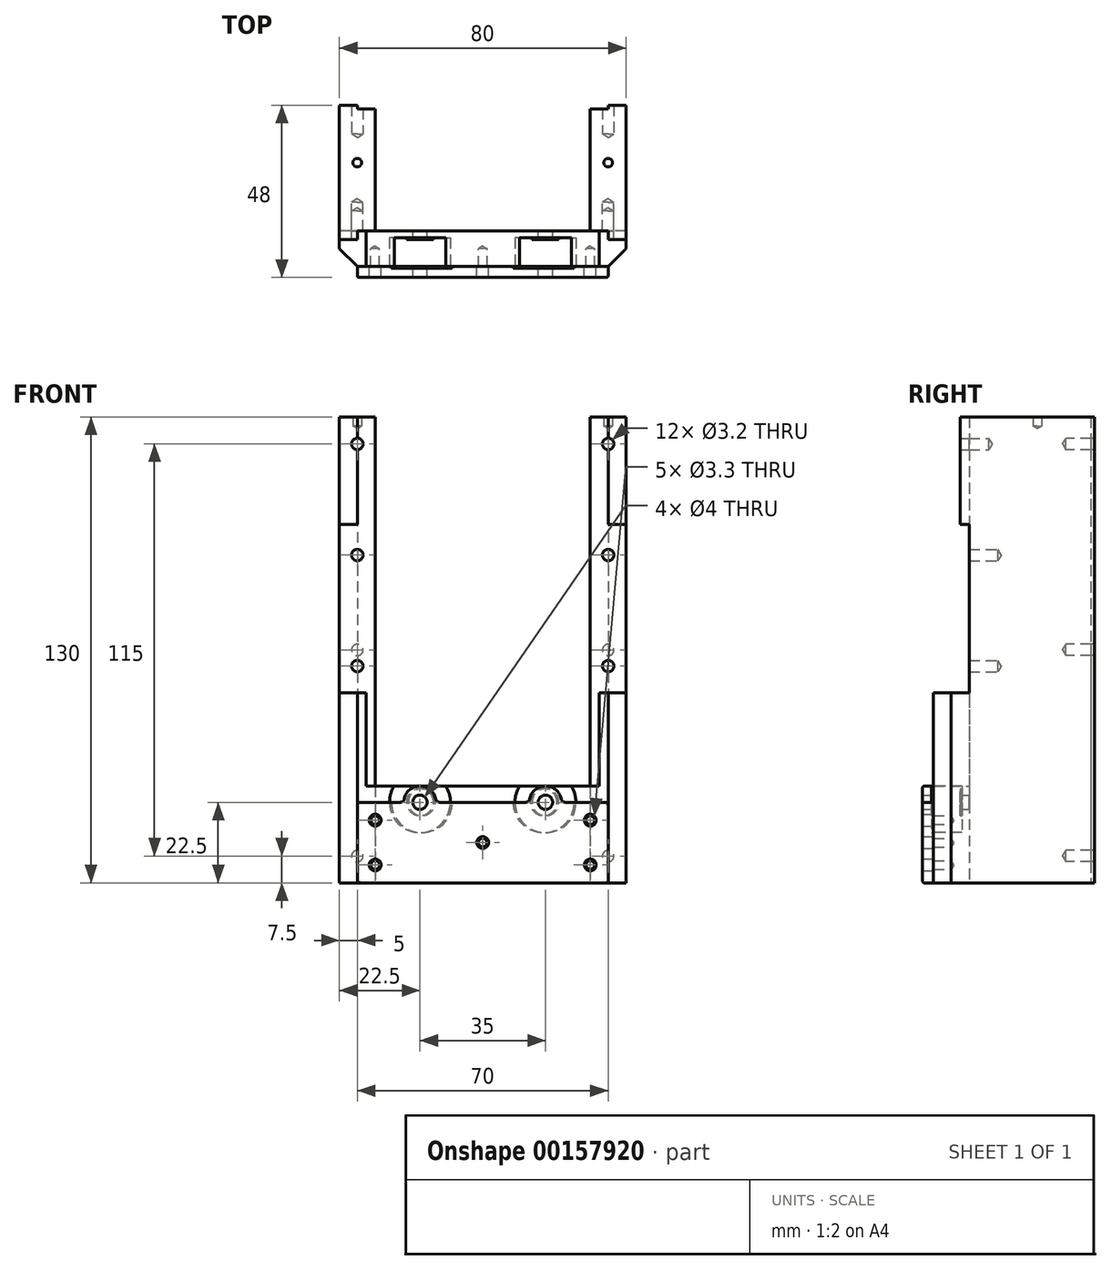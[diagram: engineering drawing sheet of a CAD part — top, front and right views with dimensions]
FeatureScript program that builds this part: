
annotation { "Feature Type Name" : "Feature", "Feature Type Description" : "" }
export const myFeature = defineFeature(function(context is Context, id is Id, definition is map)
    precondition{}
    {
        {
            var Q0;
            Q0=qCreatedBy(makeId("Top.planeOp"),FACE);
            cPlane(context, id + "F0", {"entities" : qUnion([Q0]), "cplaneType" : CPlaneType.OFFSET, "offset" : 90 * mm, "oppositeDirection" : true, "width" : 150 * mm, "height" : 150 * mm});
        }
        {
            var Q0;
            Q0=qCreatedBy(id+"F0.planeOp",FACE);
            var sketch = newSketch(context, id + "F1", { "sketchPlane" : qUnion([Q0])});
            skLineSegment(sketch, "E0", {"start": v(-30, -14.78) * mm, "end": v(30, -14.78) * mm});
            skLineSegment(sketch, "E1", {"start": v(40, -24.78) * mm, "end": v(-40, -24.78) * mm});
            skLineSegment(sketch, "E2.0", {"start": v(40, 20.22) * mm, "end": v(35, 20.22) * mm});
            skLineSegment(sketch, "E3", {"start": v(35, 20.22) * mm, "end": v(35, 19.22) * mm});
            skLineSegment(sketch, "E4", {"start": v(35, 19.22) * mm, "end": v(30, 19.22) * mm});
            skLineSegment(sketch, "E5", {"start": v(30, -14.78) * mm, "end": v(30, 19.22) * mm});
            skLineSegment(sketch, "E6.MirrorCS", {"start": v(-30, -14.78) * mm, "end": v(-30, 19.22) * mm});
            skLineSegment(sketch, "E7.MirrorCS", {"start": v(-40, 20.22) * mm, "end": v(-35, 20.22) * mm});
            skLineSegment(sketch, "E8", {"start": v(40, 20.22) * mm, "end": v(40, -24.78) * mm});
            skLineSegment(sketch, "E9", {"start": v(-30, 19.22) * mm, "end": v(-35, 19.22) * mm});
            skLineSegment(sketch, "E10", {"start": v(-35, 19.22) * mm, "end": v(-35, 20.22) * mm});
            skLineSegment(sketch, "E11", {"start": v(-40, 20.22) * mm, "end": v(-40, -24.78) * mm});
            skSolve(sketch);
        }
        {
            var Q0;
            Q0 = qSketchRegion(id + "F1", true);
            extrude(context, id + "F2", {"entities" : qUnion([Q0]), "depth" : 27 * mm});
        }
        {
            var Q0;
            Q0=makeQuery(id+"F2.opExtrude","CAP_FACE",FACE,{"disambiguationData":[OSD([sQuery(id+"F1.wireOp",EDGE,"E0"),sQuery(id+"F1.wireOp",EDGE,"E1"),sQuery(id+"F1.wireOp",EDGE,"E2.0"),sQuery(id+"F1.wireOp",EDGE,"E3"),sQuery(id+"F1.wireOp",EDGE,"E4"),sQuery(id+"F1.wireOp",EDGE,"E5"),sQuery(id+"F1.wireOp",EDGE,"E6.MirrorCS"),sQuery(id+"F1.wireOp",EDGE,"E7.MirrorCS"),sQuery(id+"F1.wireOp",EDGE,"E8"),sQuery(id+"F1.wireOp",EDGE,"E9"),sQuery(id+"F1.wireOp",EDGE,"E10"),sQuery(id+"F1.wireOp",EDGE,"E11")])],"isStart":false});
            var sketch = newSketch(context, id + "F3", { "sketchPlane" : qUnion([Q0])});
            skLineSegment(sketch, "E12.0", {"start": v(40, 20.22) * mm, "end": v(40, -24.78) * mm});
            skLineSegment(sketch, "E13.0", {"start": v(40, 20.22) * mm, "end": v(35, 20.22) * mm});
            skLineSegment(sketch, "E14.0", {"start": v(35, 19.22) * mm, "end": v(30, 19.22) * mm});
            skLineSegment(sketch, "E15", {"start": v(35, 20.22) * mm, "end": v(35, 19.22) * mm});
            skLineSegment(sketch, "E16.0", {"start": v(30, -14.78) * mm, "end": v(30, 19.22) * mm});
            skLineSegment(sketch, "E17", {"start": v(40, -24.78) * mm, "end": v(32.5, -24.78) * mm});
            skLineSegment(sketch, "E18", {"start": v(32.5, -24.78) * mm, "end": v(32.5, -14.78) * mm});
            skLineSegment(sketch, "E19.MirrorCS", {"start": v(-30, -14.78) * mm, "end": v(-30, 19.22) * mm});
            skLineSegment(sketch, "E20.MirrorCS", {"start": v(-35, 19.22) * mm, "end": v(-30, 19.22) * mm});
            skLineSegment(sketch, "E21.MirrorCS", {"start": v(-40, 20.22) * mm, "end": v(-35, 20.22) * mm});
            skLineSegment(sketch, "E22.MirrorCS", {"start": v(-40, 20.22) * mm, "end": v(-40, -24.78) * mm});
            skLineSegment(sketch, "E23.MirrorCS", {"start": v(-40, -24.78) * mm, "end": v(-32.5, -24.78) * mm});
            skLineSegment(sketch, "E24.MirrorCS", {"start": v(-32.5, -24.78) * mm, "end": v(-32.5, -14.78) * mm});
            skLineSegment(sketch, "E25", {"start": v(-35, 20.22) * mm, "end": v(-35, 19.22) * mm});
            skLineSegment(sketch, "E26", {"start": v(-32.5, -14.78) * mm, "end": v(32.5, -14.78) * mm});
            skSolve(sketch);
        }
        {
            var Q0;
            Q0 = qSketchRegion(id + "F3", true);
            extrude(context, id + "F4", {"entities" : qUnion([Q0]), "operationType" : NewBodyOperationType.ADD, "depth" : 26 * mm});
        }
        {
            var Q0;
            Q0=makeQuery(id+"F4.opExtrude","CAP_FACE",FACE,{"disambiguationData":[OSD([sQuery(id+"F3.wireOp",EDGE,"E19.MirrorCS"),sQuery(id+"F3.wireOp",EDGE,"E20.MirrorCS"),sQuery(id+"F3.wireOp",EDGE,"E21.MirrorCS"),sQuery(id+"F3.wireOp",EDGE,"E22.MirrorCS"),sQuery(id+"F3.wireOp",EDGE,"E23.MirrorCS"),sQuery(id+"F3.wireOp",EDGE,"E24.MirrorCS"),sQuery(id+"F3.wireOp",EDGE,"E25"),sQuery(id+"F3.wireOp",EDGE,"E26")])],"isStart":false});
            var sketch = newSketch(context, id + "F5", { "sketchPlane" : qUnion([Q0])});
            skLineSegment(sketch, "E27.0", {"start": v(40, 20.22) * mm, "end": v(40, -14.78) * mm});
            skLineSegment(sketch, "E28.0", {"start": v(40, 20.22) * mm, "end": v(35, 20.22) * mm});
            skLineSegment(sketch, "E29.0", {"start": v(35, 19.22) * mm, "end": v(30, 19.22) * mm});
            skLineSegment(sketch, "E30.0", {"start": v(30, -14.78) * mm, "end": v(30, 19.22) * mm});
            skLineSegment(sketch, "E31", {"start": v(35, 20.22) * mm, "end": v(35, 19.22) * mm});
            skLineSegment(sketch, "E32.MirrorCS", {"start": v(-40, 20.22) * mm, "end": v(-40, -14.78) * mm});
            skLineSegment(sketch, "E33.MirrorCS", {"start": v(-40, 20.22) * mm, "end": v(-35, 20.22) * mm});
            skLineSegment(sketch, "E34.MirrorCS", {"start": v(-35, 19.22) * mm, "end": v(-30, 19.22) * mm});
            skLineSegment(sketch, "E35.MirrorCS", {"start": v(-30, -14.78) * mm, "end": v(-30, 19.22) * mm});
            skLineSegment(sketch, "E36.MirrorCS", {"start": v(-35, 20.22) * mm, "end": v(-35, 19.22) * mm});
            skLineSegment(sketch, "E37", {"start": v(40, -14.78) * mm, "end": v(30, -14.78) * mm});
            skPoint(sketch, "E38.orphan", {"position": v(40, -24.78) * mm});
            skPoint(sketch, "E39.orphan", {"position": v(-40, -24.78) * mm});
            skLineSegment(sketch, "E40.trimOffspring", {"start": v(-30, -14.78) * mm, "end": v(-40, -14.78) * mm});
            skSolve(sketch);
        }
        {
            var Q0;
            Q0 = qSketchRegion(id + "F5", true);
            extrude(context, id + "F6", {"entities" : qUnion([Q0]), "operationType" : NewBodyOperationType.ADD, "depth" : 47 * mm});
        }
        {
            var Q0;
            Q0=makeQuery(id+"F6.opExtrude","CAP_FACE",FACE,{"disambiguationData":[OSD([sQuery(id+"F5.wireOp",EDGE,"E27.0"),sQuery(id+"F5.wireOp",EDGE,"E28.0"),sQuery(id+"F5.wireOp",EDGE,"E29.0"),sQuery(id+"F5.wireOp",EDGE,"E30.0"),sQuery(id+"F5.wireOp",EDGE,"E31"),sQuery(id+"F5.wireOp",EDGE,"E37")])],"isStart":false});
            var sketch = newSketch(context, id + "F7", { "sketchPlane" : qUnion([Q0])});
            skLineSegment(sketch, "E41.0", {"start": v(40, 20.22) * mm, "end": v(35, 20.22) * mm});
            skLineSegment(sketch, "E42.0", {"start": v(35, 19.22) * mm, "end": v(30, 19.22) * mm});
            skLineSegment(sketch, "E43.0", {"start": v(30, -14.78) * mm, "end": v(30, 19.22) * mm});
            skLineSegment(sketch, "E44.0", {"start": v(35, -14.78) * mm, "end": v(30, -14.78) * mm});
            skLineSegment(sketch, "E45", {"start": v(35, 20.22) * mm, "end": v(35, 19.22) * mm});
            skLineSegment(sketch, "E46", {"start": v(35, -14.78) * mm, "end": v(35, -17.28) * mm});
            skLineSegment(sketch, "E47", {"start": v(35, -17.28) * mm, "end": v(40, -17.28) * mm});
            skPoint(sketch, "E48.orphan", {"position": v(40, -14.78) * mm});
            skLineSegment(sketch, "E49", {"start": v(40, 20.22) * mm, "end": v(40, -17.28) * mm});
            skLineSegment(sketch, "E50.MirrorCS", {"start": v(-35, 19.22) * mm, "end": v(-30, 19.22) * mm});
            skLineSegment(sketch, "E51.MirrorCS", {"start": v(-35, 20.22) * mm, "end": v(-35, 19.22) * mm});
            skLineSegment(sketch, "E52.MirrorCS", {"start": v(-40, 20.22) * mm, "end": v(-35, 20.22) * mm});
            skLineSegment(sketch, "E53.MirrorCS", {"start": v(-40, 20.22) * mm, "end": v(-40, -17.28) * mm});
            skLineSegment(sketch, "E54.MirrorCS", {"start": v(-35, -17.28) * mm, "end": v(-40, -17.28) * mm});
            skLineSegment(sketch, "E55.MirrorCS", {"start": v(-35, -14.78) * mm, "end": v(-35, -17.28) * mm});
            skLineSegment(sketch, "E56.MirrorCS", {"start": v(-35, -14.78) * mm, "end": v(-30, -14.78) * mm});
            skLineSegment(sketch, "E57.MirrorCS", {"start": v(-30, -14.78) * mm, "end": v(-30, 19.22) * mm});
            skSolve(sketch);
        }
        {
            var Q0;
            Q0 = qSketchRegion(id + "F7", true);
            extrude(context, id + "F8", {"entities" : qUnion([Q0]), "operationType" : NewBodyOperationType.ADD, "depth" : 30 * mm});
        }
        {
            var Q0;
            Q0=makeQuery(id+"F4.boolean.opBoolean","MERGE",FACE,{"derivedFrom":[makeQuery(id+"F2.opExtrude","SWEPT_FACE",FACE,{"disambiguationData":[OSD([sQuery(id+"F1.wireOp",EDGE,"E1")])]}),makeQuery(id+"F4.opExtrude","SWEPT_FACE",FACE,{"disambiguationData":[OSD([sQuery(id+"F3.wireOp",EDGE,"E17")])]}),makeQuery(id+"F4.opExtrude","SWEPT_FACE",FACE,{"disambiguationData":[OSD([sQuery(id+"F3.wireOp",EDGE,"E23.MirrorCS")])]})]});
            var sketch = newSketch(context, id + "F9", { "sketchPlane" : qUnion([Q0])});
            skCircle(sketch, "E58", {"center": v(17.5, -67.5) * mm, "radius": 8.5 * mm});
            skCircle(sketch, "E59.MirrorC", {"center": v(-17.5, -67.5) * mm, "radius": 8.5 * mm});
            skSolve(sketch);
        }
        {
            var Q0;
            Q0 = qSketchRegion(id + "F9", true);
            extrude(context, id + "F10", {"entities" : qUnion([Q0]), "operationType" : NewBodyOperationType.REMOVE, "oppositeDirection" : true, "depth" : 8 * mm});
        }
        {
            var Q0;
            Q0=makeQuery(id+"F10.boolean.opBoolean","COPY",FACE,{"derivedFrom":makeQuery(id+"F10.opExtrude","CAP_FACE",FACE,{"disambiguationData":[OSD([sQuery(id+"F9.wireOp",EDGE,"E58")])],"isStart":false})});
            var sketch = newSketch(context, id + "F11", { "sketchPlane" : qUnion([Q0])});
            skCircle(sketch, "E60", {"center": v(17.5, -67.5) * mm, "radius": 2 * mm});
            skCircle(sketch, "E61", {"center": v(17.5, -67.5) * mm, "radius": 3.75 * mm});
            skCircle(sketch, "E62.MirrorC", {"center": v(-17.5, -67.5) * mm, "radius": 3.75 * mm});
            skCircle(sketch, "E63.MirrorC", {"center": v(-17.5, -67.5) * mm, "radius": 2 * mm});
            skSolve(sketch);
        }
        {
            var Q0;
            Q0 = qSketchRegion(id + "F11", true);
            extrude(context, id + "F12", {"entities" : qUnion([Q0]), "operationType" : NewBodyOperationType.ADD, "depth" : 0.5 * mm});
        }
        {
            var Q0;
            Q0=makeQuery(id+"F12.boolean.opBoolean","SPLIT",FACE,{"disambiguationData":[TD([makeQuery(id+"F12.opExtrude","SWEPT_FACE",FACE,{"disambiguationData":[OSD([sQuery(id+"F11.wireOp",EDGE,"E60")])]})])],"derivedFrom":makeQuery(id+"F10.boolean.opBoolean","COPY",FACE,{"derivedFrom":makeQuery(id+"F10.opExtrude","CAP_FACE",FACE,{"disambiguationData":[OSD([sQuery(id+"F9.wireOp",EDGE,"E58")])],"isStart":false})})});
            var Q1;
            Q1=makeQuery(id+"F12.boolean.opBoolean","SPLIT",FACE,{"disambiguationData":[TD([makeQuery(id+"F12.opExtrude","SWEPT_FACE",FACE,{"disambiguationData":[OSD([sQuery(id+"F11.wireOp",EDGE,"E63.MirrorC")])]})])],"derivedFrom":makeQuery(id+"F10.boolean.opBoolean","COPY",FACE,{"derivedFrom":makeQuery(id+"F10.opExtrude","CAP_FACE",FACE,{"disambiguationData":[OSD([sQuery(id+"F9.wireOp",EDGE,"E59.MirrorC")])],"isStart":false})})});
            extrude(context, id + "F13", {"entities" : qUnion([Q0, Q1]), "operationType" : NewBodyOperationType.REMOVE, "oppositeDirection" : true, "depth" : 25 * mm});
        }
        {
            var Q0;
            Q0=makeQuery(id+"F4.boolean.opBoolean","MERGE",EDGE,{"derivedFrom":[makeQuery(id+"F2.opExtrude","SWEPT_EDGE",EDGE,{"disambiguationData":[OSD([sQuery(id+"F1.wireOp",EDGE,"E1"),sQuery(id+"F1.wireOp",EDGE,"E8")])]}),makeQuery(id+"F4.opExtrude","SWEPT_EDGE",EDGE,{"disambiguationData":[OSD([sQuery(id+"F3.wireOp",EDGE,"E12.0"),sQuery(id+"F3.wireOp",EDGE,"E17")])]})]});
            var Q1;
            Q1=makeQuery(id+"F4.boolean.opBoolean","MERGE",EDGE,{"derivedFrom":[makeQuery(id+"F2.opExtrude","SWEPT_EDGE",EDGE,{"disambiguationData":[OSD([sQuery(id+"F1.wireOp",EDGE,"E1"),sQuery(id+"F1.wireOp",EDGE,"E11")])]}),makeQuery(id+"F4.opExtrude","SWEPT_EDGE",EDGE,{"disambiguationData":[OSD([sQuery(id+"F3.wireOp",EDGE,"E22.MirrorCS"),sQuery(id+"F3.wireOp",EDGE,"E23.MirrorCS")])]})]});
            chamfer(context, id + "F14", {"entities" : qUnion([Q0, Q1]), "width" : 5 * mm, "tangentPropagation" : true});
        }
        {
            var Q0;
            Q0=makeQuery(id+"F14.opChamfer","SPLIT",FACE,{"disambiguationData":[OD(2.0)],"derivedFrom":makeQuery(id+"F4.boolean.opBoolean","MERGE",FACE,{"derivedFrom":[makeQuery(id+"F2.opExtrude","SWEPT_FACE",FACE,{"disambiguationData":[OSD([sQuery(id+"F1.wireOp",EDGE,"E1")])]}),makeQuery(id+"F4.opExtrude","SWEPT_FACE",FACE,{"disambiguationData":[OSD([sQuery(id+"F3.wireOp",EDGE,"E17")])]}),makeQuery(id+"F4.opExtrude","SWEPT_FACE",FACE,{"disambiguationData":[OSD([sQuery(id+"F3.wireOp",EDGE,"E23.MirrorCS")])]})]})});
            var sketch = newSketch(context, id + "F15", { "sketchPlane" : qUnion([Q0])});
            skCircle(sketch, "E64.0", {"center": v(-17.5, -67.5) * mm, "radius": 2 * mm});
            skCircle(sketch, "E65.0", {"center": v(17.5, -67.5) * mm, "radius": 2 * mm});
            skLineSegment(sketch, "E66", {"start": v(-35, -90) * mm, "end": v(35, -90) * mm});
            skLineSegment(sketch, "E67", {"start": v(35, -90) * mm, "end": v(35, -67.5) * mm});
            skPoint(sketch, "E68.orphan", {"position": v(-35, -70.15) * mm});
            skPoint(sketch, "E69.orphan", {"position": v(35, -70.15) * mm});
            skLineSegment(sketch, "E70.MirrorCS", {"start": v(-35, -90) * mm, "end": v(-35, -67.5) * mm});
            skLineSegment(sketch, "E71", {"start": v(-35, -67.5) * mm, "end": v(-22, -67.5) * mm});
            skArc(sketch, "E72", {"start": v(22, -67.5) * mm, "mid": v(17.5, -63) * mm, "end": v(13, -67.5) * mm});
            skArc(sketch, "E73.MirrorC", {"start": v(-22, -67.5) * mm, "mid": v(-17.5, -63) * mm, "end": v(-13, -67.5) * mm});
            skLineSegment(sketch, "E74.trimOffspring", {"start": v(-13, -67.5) * mm, "end": v(13, -67.5) * mm});
            skLineSegment(sketch, "E75.trimOffspring", {"start": v(19.5, -67.5) * mm, "end": v(35, -67.5) * mm});
            skSolve(sketch);
        }
        {
            var Q0;
            Q0 = qSketchRegion(id + "F15", true);
            extrude(context, id + "F16", {"entities" : qUnion([Q0]), "depth" : 3 * mm});
        }
        {
            var Q0;
            Q0=makeQuery(id+"F16.opExtrude","CAP_FACE",FACE,{"disambiguationData":[OSD([sQuery(id+"F15.wireOp",EDGE,"E64.0"),sQuery(id+"F15.wireOp",EDGE,"E65.0"),sQuery(id+"F15.wireOp",EDGE,"2QbMT2nW-IAl8-gtQJ-p2Iz-kW7memZSLAfn"),sQuery(id+"F15.wireOp",EDGE,"XE8XkPs4-BKOY-PGEx-oHFn-p07Z73GzMPRD"),sQuery(id+"F15.wireOp",EDGE,"nKjhpJZj-CjEx-POrg-9XYW-dTicIIr4c24b"),sQuery(id+"F15.wireOp",EDGE,"gEchJP0V-37SP-750J-l0El-UBUOQwK3IVrr"),sQuery(id+"F15.wireOp",EDGE,"E66"),sQuery(id+"F15.wireOp",EDGE,"h1sLuy6x-Yomr-532m-xEHi-TijXeizuQsZO"),sQuery(id+"F15.wireOp",EDGE,"mAC8uAtB-FTIW-m3pB-ZDK8-pyVDg6E0Xd48"),sQuery(id+"F15.wireOp",EDGE,"HEceFARl-BTcW-MZeQ-kquP-lKw35DMknYV2")])],"isStart":false});
            var sketch = newSketch(context, id + "F17", { "sketchPlane" : qUnion([Q0])});
            skCircle(sketch, "E76", {"center": v(0, -78.75) * mm, "radius": 2 * mm});
            skCircle(sketch, "E77", {"center": v(30, -85) * mm, "radius": 2 * mm});
            skCircle(sketch, "E78", {"center": v(30, -72.5) * mm, "radius": 2 * mm});
            skCircle(sketch, "E79.MirrorC", {"center": v(-30, -72.5) * mm, "radius": 2 * mm});
            skCircle(sketch, "E80.MirrorC", {"center": v(-30, -85) * mm, "radius": 2 * mm});
            skSolve(sketch);
        }
        {
            var Q0;
            Q0=makeQuery(id+"F4.boolean.opBoolean","MERGE",FACE,{"derivedFrom":[makeQuery(id+"F2.opExtrude","SWEPT_FACE",FACE,{"disambiguationData":[OSD([sQuery(id+"F1.wireOp",EDGE,"E1")])]}),makeQuery(id+"F4.opExtrude","SWEPT_FACE",FACE,{"disambiguationData":[OSD([sQuery(id+"F3.wireOp",EDGE,"E17")])]}),makeQuery(id+"F4.opExtrude","SWEPT_FACE",FACE,{"disambiguationData":[OSD([sQuery(id+"F3.wireOp",EDGE,"E23.MirrorCS")])]})]});
            var sketch = newSketch(context, id + "F18", { "sketchPlane" : qUnion([Q0])});
            skCircle(sketch, "E81", {"center": v(17, -67.5) * mm, "radius": 3.75 * mm});
            skCircle(sketch, "E82", {"center": v(17, -67.5) * mm, "radius": 8.5 * mm});
            skCircle(sketch, "E83.MirrorC", {"center": v(-17, -67.5) * mm, "radius": 8.5 * mm});
            skCircle(sketch, "E84.MirrorC", {"center": v(-17, -67.5) * mm, "radius": 3.75 * mm});
            skSolve(sketch);
        }
        {
            var Q0;
            Q0 = qSketchRegion(id + "F18", true);
            extrude(context, id + "F19", {"entities" : qUnion([Q0]), "operationType" : NewBodyOperationType.REMOVE, "depth" : 0.5 * mm});
        }
        {
            var Q0;
            Q0=makeQuery(id+"F8.boolean.opBoolean","MERGE",FACE,{"derivedFrom":[makeQuery(id+"F6.boolean.opBoolean","MERGE",FACE,{"derivedFrom":[makeQuery(id+"F4.boolean.opBoolean","MERGE",FACE,{"derivedFrom":[makeQuery(id+"F2.opExtrude","SWEPT_FACE",FACE,{"disambiguationData":[OSD([sQuery(id+"F1.wireOp",EDGE,"E7.MirrorCS")])]}),makeQuery(id+"F4.opExtrude","SWEPT_FACE",FACE,{"disambiguationData":[OSD([sQuery(id+"F3.wireOp",EDGE,"E21.MirrorCS")])]})]}),makeQuery(id+"F6.opExtrude","SWEPT_FACE",FACE,{"disambiguationData":[OSD([sQuery(id+"F5.wireOp",EDGE,"E33.MirrorCS")])]})]}),makeQuery(id+"F8.opExtrude","SWEPT_FACE",FACE,{"disambiguationData":[OSD([sQuery(id+"F7.wireOp",EDGE,"E52.MirrorCS")])]})]});
            var sketch = newSketch(context, id + "F20", { "sketchPlane" : qUnion([Q0])});
            skCircle(sketch, "E85", {"center": v(35, -25) * mm, "radius": 3.68 * mm});
            skCircle(sketch, "E86", {"center": v(35, 32.5) * mm, "radius": 3.47 * mm});
            skCircle(sketch, "E87.MirrorC", {"center": v(-35, 32.5) * mm, "radius": 3.47 * mm});
            skCircle(sketch, "E88.MirrorC", {"center": v(-35, -25) * mm, "radius": 3.68 * mm});
            skLineSegment(sketch, "E89", {"start": v(-35, -25) * mm, "end": v(35, -25) * mm});
            skCircle(sketch, "E90.MirrorC", {"center": v(-35, -82.5) * mm, "radius": 3.47 * mm});
            skCircle(sketch, "E91.MirrorC", {"center": v(35, -82.5) * mm, "radius": 3.47 * mm});
            skSolve(sketch);
        }
        {
            var Q0;
            Q0=sQuery(id+"F20.wireOp",VERTEX,"E86.center");
            var Q1;
            Q1=sQuery(id+"F20.wireOp",VERTEX,"E85.center");
            var Q2;
            Q2=sQuery(id+"F20.wireOp",VERTEX,"4epNUfqm-IPoI-M6fA-UF52-nUd3HmOOQX4Y.center");
            var Q3;
            Q3=sQuery(id+"F20.wireOp",VERTEX,"a63e8368-61fe-4b29-9349-38a90727234b0.MirrorC.center");
            var Q4;
            Q4=sQuery(id+"F20.wireOp",VERTEX,"E88.MirrorC.center");
            var Q5;
            Q5=sQuery(id+"F20.wireOp",VERTEX,"E87.MirrorC.center");
            var Q6;
            Q6=sQuery(id+"F20.wireOp",VERTEX,"E90.MirrorC.center");
            var Q7;
            Q7=sQuery(id+"F20.wireOp",VERTEX,"E91.MirrorC.center");
            var Q8;
            Q8=makeQuery(id+"F2.opExtrude","SWEPT_BODY",BODY,{"disambiguationData":[OSD([sQuery(id+"F1.wireOp",EDGE,"E0"),sQuery(id+"F1.wireOp",EDGE,"E1"),sQuery(id+"F1.wireOp",EDGE,"E2.0"),sQuery(id+"F1.wireOp",EDGE,"E3"),sQuery(id+"F1.wireOp",EDGE,"E4"),sQuery(id+"F1.wireOp",EDGE,"E5"),sQuery(id+"F1.wireOp",EDGE,"E6.MirrorCS"),sQuery(id+"F1.wireOp",EDGE,"E7.MirrorCS"),sQuery(id+"F1.wireOp",EDGE,"E8"),sQuery(id+"F1.wireOp",EDGE,"E9"),sQuery(id+"F1.wireOp",EDGE,"E10"),sQuery(id+"F1.wireOp",EDGE,"E11")])]});
            hole(context, id + "F21", {"style" : HoleStyle.SIMPLE, "endStyle" : HoleEndStyle.BLIND, "standardTappedOrClearance" : lookupTablePath({ "standard" : "ISO", "engagement" : "75%", "pitch" : "0.75 mm", "size" : "M4", "type" : "Tapped" }), "standardBlindInLast" : lookupTablePath({ "standard" : "ISO", "engagement" : "75%", "pitch" : "0.75 mm", "size" : "M4", "type" : "Tapped" }), "holeDiameter" : 3.2 * mm, "holeDepth" : 8 * mm, "locations" : qUnion([Q0, Q1, Q2, Q3, Q4, Q5, Q6, Q7]), "scope" : qUnion([Q8]), "startStyle" : HoleStartStyle.SKETCH});
        }
        {
            var Q0;
            {var subQ0=sQuery(id+"F3.wireOp",EDGE,"E26");Q0=makeQuery(id+"F8.boolean.opBoolean","MERGE",FACE,{"derivedFrom":[makeQuery(id+"F6.boolean.opBoolean","MERGE",FACE,{"derivedFrom":[makeQuery(id+"F4.opExtrude","SWEPT_FACE",FACE,{"disambiguationData":[OSD([subQ0]),TDD([makeQuery(id+"F3.imprint","IMPRINT",EDGE,{"disambiguationData":[TD([[makeQuery(id+"F3.imprint","INTERSECT",VERTEX,{"derivedFrom":[sQuery(id+"F3.wireOp",EDGE,"E19.MirrorCS"),subQ0]}),1.0]])],"derivedFrom":subQ0})])]}),makeQuery(id+"F6.opExtrude","SWEPT_FACE",FACE,{"disambiguationData":[OSD([sQuery(id+"F5.wireOp",EDGE,"E40.trimOffspring")])]})]}),makeQuery(id+"F8.opExtrude","SWEPT_FACE",FACE,{"disambiguationData":[OSD([sQuery(id+"F7.wireOp",EDGE,"E56.MirrorCS")])]})]});}
            var sketch = newSketch(context, id + "F22", { "sketchPlane" : qUnion([Q0])});
            skCircle(sketch, "E92", {"center": v(-35, 1.5) * mm, "radius": 1.13 * mm});
            skCircle(sketch, "E93.MirrorC", {"center": v(35, 1.5) * mm, "radius": 1.13 * mm});
            skCircle(sketch, "E94", {"center": v(-35, -29.5) * mm, "radius": 1.45 * mm});
            skCircle(sketch, "E95.MirrorC", {"center": v(35, -29.5) * mm, "radius": 1.45 * mm});
            skSolve(sketch);
        }
        {
            var Q0;
            Q0=makeQuery(id+"F8.opExtrude","SWEPT_FACE",FACE,{"disambiguationData":[OSD([sQuery(id+"F7.wireOp",EDGE,"E54.MirrorCS")])]});
            var sketch = newSketch(context, id + "F23", { "sketchPlane" : qUnion([Q0])});
            skCircle(sketch, "E96", {"center": v(-35, 32.5) * mm, "radius": 2.04 * mm});
            skCircle(sketch, "E97.MirrorC", {"center": v(35, 32.5) * mm, "radius": 2.04 * mm});
            skSolve(sketch);
        }
        {
            var Q0;
            Q0=sQuery(id+"F23.wireOp",VERTEX,"E96.center");
            var Q1;
            Q1=sQuery(id+"F23.wireOp",VERTEX,"E97.MirrorC.center");
            var Q2;
            Q2=sQuery(id+"F22.wireOp",VERTEX,"E92.center");
            var Q3;
            Q3=sQuery(id+"F22.wireOp",VERTEX,"E93.MirrorC.center");
            var Q4;
            Q4=sQuery(id+"F22.wireOp",VERTEX,"E94.center");
            var Q5;
            Q5=sQuery(id+"F22.wireOp",VERTEX,"E95.MirrorC.center");
            var Q6;
            Q6=makeQuery(id+"F2.opExtrude","SWEPT_BODY",BODY,{"disambiguationData":[OSD([sQuery(id+"F1.wireOp",EDGE,"E0"),sQuery(id+"F1.wireOp",EDGE,"E1"),sQuery(id+"F1.wireOp",EDGE,"E2.0"),sQuery(id+"F1.wireOp",EDGE,"E3"),sQuery(id+"F1.wireOp",EDGE,"E4"),sQuery(id+"F1.wireOp",EDGE,"E5"),sQuery(id+"F1.wireOp",EDGE,"E6.MirrorCS"),sQuery(id+"F1.wireOp",EDGE,"E7.MirrorCS"),sQuery(id+"F1.wireOp",EDGE,"E8"),sQuery(id+"F1.wireOp",EDGE,"E9"),sQuery(id+"F1.wireOp",EDGE,"E10"),sQuery(id+"F1.wireOp",EDGE,"E11")])]});
            hole(context, id + "F24", {"style" : HoleStyle.SIMPLE, "endStyle" : HoleEndStyle.BLIND, "standardTappedOrClearance" : lookupTablePath({ "standard" : "ISO", "engagement" : "75%", "pitch" : "0.75 mm", "size" : "M4", "type" : "Tapped" }), "standardBlindInLast" : lookupTablePath({ "standard" : "ISO", "engagement" : "75%", "pitch" : "0.75 mm", "size" : "M4", "type" : "Tapped" }), "holeDiameter" : 3.2 * mm, "holeDepth" : 8 * mm, "locations" : qUnion([Q0, Q1, Q2, Q3, Q4, Q5]), "scope" : qUnion([Q6]), "startStyle" : HoleStartStyle.SKETCH});
        }
        {
            var Q0;
            Q0=makeQuery(id+"F16.opExtrude","SWEPT_EDGE",EDGE,{"disambiguationData":[OSD([sQuery(id+"F15.wireOp",EDGE,"E73.MirrorC"),sQuery(id+"F15.wireOp",EDGE,"E74.trimOffspring")])]});
            var Q1;
            Q1=makeQuery(id+"F16.opExtrude","SWEPT_EDGE",EDGE,{"disambiguationData":[OSD([sQuery(id+"F15.wireOp",EDGE,"E72"),sQuery(id+"F15.wireOp",EDGE,"E75.trimOffspring")])]});
            var Q2;
            Q2=makeQuery(id+"F16.opExtrude","SWEPT_EDGE",EDGE,{"disambiguationData":[OSD([sQuery(id+"F15.wireOp",EDGE,"E72"),sQuery(id+"F15.wireOp",EDGE,"E74.trimOffspring")])]});
            var Q3;
            Q3=makeQuery(id+"F16.opExtrude","SWEPT_EDGE",EDGE,{"disambiguationData":[OSD([sQuery(id+"F15.wireOp",EDGE,"E71"),sQuery(id+"F15.wireOp",EDGE,"E73.MirrorC")])]});
            fillet(context, id + "F25", {"entities" : qUnion([Q0, Q1, Q2, Q3]), "radius" : 1 * mm, "tangentPropagation" : true, "allowEdgeOverflow" : false});
        }
        {
            var Q0;
            Q0=makeQuery(id+"F16.opExtrude","CAP_EDGE",EDGE,{"disambiguationData":[OSD([sQuery(id+"F15.wireOp",EDGE,"E71")])],"isStart":false});
            var Q1;
            {var subQ0=sQuery(id+"F15.wireOp",EDGE,"E73.MirrorC");var subQ1=sQuery(id+"F15.wireOp",EDGE,"E71");Q1=makeQuery(id+"F25.opFillet","BLEND_EDGE",EDGE,{"blendedFrom":[makeQuery(id+"F16.opExtrude","SWEPT_EDGE",EDGE,{"disambiguationData":[OSD([subQ1,subQ0])]}),makeQuery(id+"F16.opExtrude","CAP_FACE",FACE,{"disambiguationData":[OSD([sQuery(id+"F15.wireOp",EDGE,"E64.0"),sQuery(id+"F15.wireOp",EDGE,"E65.0"),sQuery(id+"F15.wireOp",EDGE,"E66"),sQuery(id+"F15.wireOp",EDGE,"E67"),sQuery(id+"F15.wireOp",EDGE,"E70.MirrorCS"),subQ1,sQuery(id+"F15.wireOp",EDGE,"E72"),subQ0,sQuery(id+"F15.wireOp",EDGE,"E74.trimOffspring"),sQuery(id+"F15.wireOp",EDGE,"E75.trimOffspring")])],"isStart":false})],"blendedInto":[makeQuery(id+"F16.opExtrude","CAP_FACE",FACE,{"disambiguationData":[OSD([sQuery(id+"F15.wireOp",EDGE,"E64.0"),sQuery(id+"F15.wireOp",EDGE,"E65.0"),sQuery(id+"F15.wireOp",EDGE,"E66"),sQuery(id+"F15.wireOp",EDGE,"E67"),sQuery(id+"F15.wireOp",EDGE,"E70.MirrorCS"),subQ1,sQuery(id+"F15.wireOp",EDGE,"E72"),subQ0,sQuery(id+"F15.wireOp",EDGE,"E74.trimOffspring"),sQuery(id+"F15.wireOp",EDGE,"E75.trimOffspring")])],"isStart":false})]});}
            var Q2;
            Q2=makeQuery(id+"F16.opExtrude","CAP_EDGE",EDGE,{"disambiguationData":[OSD([sQuery(id+"F15.wireOp",EDGE,"E73.MirrorC")])],"isStart":false});
            var Q3;
            {var subQ0=sQuery(id+"F15.wireOp",EDGE,"E74.trimOffspring");var subQ1=sQuery(id+"F15.wireOp",EDGE,"E73.MirrorC");Q3=makeQuery(id+"F25.opFillet","BLEND_EDGE",EDGE,{"blendedFrom":[makeQuery(id+"F16.opExtrude","SWEPT_EDGE",EDGE,{"disambiguationData":[OSD([subQ1,subQ0])]}),makeQuery(id+"F16.opExtrude","CAP_FACE",FACE,{"disambiguationData":[OSD([sQuery(id+"F15.wireOp",EDGE,"E64.0"),sQuery(id+"F15.wireOp",EDGE,"E65.0"),sQuery(id+"F15.wireOp",EDGE,"E66"),sQuery(id+"F15.wireOp",EDGE,"E67"),sQuery(id+"F15.wireOp",EDGE,"E70.MirrorCS"),sQuery(id+"F15.wireOp",EDGE,"E71"),sQuery(id+"F15.wireOp",EDGE,"E72"),subQ1,subQ0,sQuery(id+"F15.wireOp",EDGE,"E75.trimOffspring")])],"isStart":false})],"blendedInto":[makeQuery(id+"F16.opExtrude","CAP_FACE",FACE,{"disambiguationData":[OSD([sQuery(id+"F15.wireOp",EDGE,"E64.0"),sQuery(id+"F15.wireOp",EDGE,"E65.0"),sQuery(id+"F15.wireOp",EDGE,"E66"),sQuery(id+"F15.wireOp",EDGE,"E67"),sQuery(id+"F15.wireOp",EDGE,"E70.MirrorCS"),sQuery(id+"F15.wireOp",EDGE,"E71"),sQuery(id+"F15.wireOp",EDGE,"E72"),subQ1,subQ0,sQuery(id+"F15.wireOp",EDGE,"E75.trimOffspring")])],"isStart":false})]});}
            var Q4;
            Q4=makeQuery(id+"F16.opExtrude","CAP_EDGE",EDGE,{"disambiguationData":[OSD([sQuery(id+"F15.wireOp",EDGE,"E67")])],"isStart":false});
            var Q5;
            Q5=makeQuery(id+"F16.opExtrude","CAP_EDGE",EDGE,{"disambiguationData":[OSD([sQuery(id+"F15.wireOp",EDGE,"E66")])],"isStart":false});
            var Q6;
            Q6=makeQuery(id+"F16.opExtrude","CAP_EDGE",EDGE,{"disambiguationData":[OSD([sQuery(id+"F15.wireOp",EDGE,"E70.MirrorCS")])],"isStart":false});
            fillet(context, id + "F26", {"entities" : qUnion([Q0, Q1, Q2, Q3, Q4, Q5, Q6]), "radius" : 0.5 * mm, "tangentPropagation" : true, "allowEdgeOverflow" : false});
        }
        {
            var Q0;
            Q0=sQuery(id+"F17.wireOp",VERTEX,"E78.center");
            var Q1;
            Q1=sQuery(id+"F17.wireOp",VERTEX,"E76.center");
            var Q2;
            Q2=sQuery(id+"F17.wireOp",VERTEX,"E77.center");
            var Q3;
            Q3=sQuery(id+"F17.wireOp",VERTEX,"E80.MirrorC.center");
            var Q4;
            Q4=sQuery(id+"F17.wireOp",VERTEX,"E79.MirrorC.center");
            var Q5;
            Q5=makeQuery(id+"F16.opExtrude","SWEPT_BODY",BODY,{"disambiguationData":[OSD([sQuery(id+"F15.wireOp",EDGE,"E64.0"),sQuery(id+"F15.wireOp",EDGE,"E65.0"),sQuery(id+"F15.wireOp",EDGE,"E66"),sQuery(id+"F15.wireOp",EDGE,"E67"),sQuery(id+"F15.wireOp",EDGE,"E70.MirrorCS"),sQuery(id+"F15.wireOp",EDGE,"E71"),sQuery(id+"F15.wireOp",EDGE,"E72"),sQuery(id+"F15.wireOp",EDGE,"E73.MirrorC"),sQuery(id+"F15.wireOp",EDGE,"E74.trimOffspring"),sQuery(id+"F15.wireOp",EDGE,"E75.trimOffspring")])]});
            hole(context, id + "F27", {"style" : HoleStyle.SIMPLE, "endStyle" : HoleEndStyle.THROUGH, "standardTappedOrClearance" : lookupTablePath({ "standard" : "ISO", "fit" : "Normal", "size" : "M3", "type" : "Clearance" }), "standardBlindInLast" : lookupTablePath({ "fit" : "Standard", "standard" : "ISO", "size" : "M3", "type" : "Clearance" }), "holeDiameter" : 3.3 * mm, "locations" : qUnion([Q0, Q1, Q2, Q3, Q4]), "scope" : qUnion([Q5]), "isTappedThrough" : true, "startStyle" : HoleStartStyle.SKETCH});
        }
        {
            var Q0;
            Q0=sQuery(id+"F17.wireOp",VERTEX,"E79.MirrorC.center");
            var Q1;
            Q1=sQuery(id+"F17.wireOp",VERTEX,"E80.MirrorC.center");
            var Q2;
            Q2=sQuery(id+"F17.wireOp",VERTEX,"E76.center");
            var Q3;
            Q3=sQuery(id+"F17.wireOp",VERTEX,"E78.center");
            var Q4;
            Q4=sQuery(id+"F17.wireOp",VERTEX,"E77.center");
            var Q5;
            Q5=makeQuery(id+"F2.opExtrude","SWEPT_BODY",BODY,{"disambiguationData":[OSD([sQuery(id+"F1.wireOp",EDGE,"E0"),sQuery(id+"F1.wireOp",EDGE,"E1"),sQuery(id+"F1.wireOp",EDGE,"E2.0"),sQuery(id+"F1.wireOp",EDGE,"E3"),sQuery(id+"F1.wireOp",EDGE,"E4"),sQuery(id+"F1.wireOp",EDGE,"E5"),sQuery(id+"F1.wireOp",EDGE,"E6.MirrorCS"),sQuery(id+"F1.wireOp",EDGE,"E7.MirrorCS"),sQuery(id+"F1.wireOp",EDGE,"E8"),sQuery(id+"F1.wireOp",EDGE,"E9"),sQuery(id+"F1.wireOp",EDGE,"E10"),sQuery(id+"F1.wireOp",EDGE,"E11")])]});
            hole(context, id + "F28", {"style" : HoleStyle.SIMPLE, "endStyle" : HoleEndStyle.BLIND, "standardTappedOrClearance" : lookupTablePath({ "standard" : "ISO", "engagement" : "75%", "pitch" : "0.6 mm", "size" : "M3", "type" : "Tapped" }), "standardBlindInLast" : lookupTablePath({ "standard" : "ISO", "engagement" : "75%", "pitch" : "0.6 mm", "size" : "M3", "type" : "Tapped" }), "holeDiameter" : 2.4 * mm, "holeDepth" : 8 * mm, "locations" : qUnion([Q0, Q1, Q2, Q3, Q4]), "scope" : qUnion([Q5]), "startStyle" : HoleStartStyle.SKETCH});
        }
        {
            var Q0;
            Q0=makeQuery(id+"F8.opExtrude","CAP_FACE",FACE,{"disambiguationData":[OSD([sQuery(id+"F7.wireOp",EDGE,"E50.MirrorCS"),sQuery(id+"F7.wireOp",EDGE,"E51.MirrorCS"),sQuery(id+"F7.wireOp",EDGE,"E52.MirrorCS"),sQuery(id+"F7.wireOp",EDGE,"E53.MirrorCS"),sQuery(id+"F7.wireOp",EDGE,"E54.MirrorCS"),sQuery(id+"F7.wireOp",EDGE,"E55.MirrorCS"),sQuery(id+"F7.wireOp",EDGE,"E56.MirrorCS"),sQuery(id+"F7.wireOp",EDGE,"E57.MirrorCS")])],"isStart":false});
            var sketch = newSketch(context, id + "F29", { "sketchPlane" : qUnion([Q0])});
            skPoint(sketch, "E98", {"position": v(-35, 4.22) * mm});
            skPoint(sketch, "E99.MirrorP", {"position": v(35, 4.22) * mm});
            skSolve(sketch);
        }
        {
            var Q0;
            Q0=sQuery(id+"F29.wireOp",VERTEX,"E98");
            var Q1;
            Q1=sQuery(id+"F29.wireOp",VERTEX,"E99.MirrorP");
            var Q2;
            Q2=makeQuery(id+"F2.opExtrude","SWEPT_BODY",BODY,{"disambiguationData":[OSD([sQuery(id+"F1.wireOp",EDGE,"E0"),sQuery(id+"F1.wireOp",EDGE,"E1"),sQuery(id+"F1.wireOp",EDGE,"E2.0"),sQuery(id+"F1.wireOp",EDGE,"E3"),sQuery(id+"F1.wireOp",EDGE,"E4"),sQuery(id+"F1.wireOp",EDGE,"E5"),sQuery(id+"F1.wireOp",EDGE,"E6.MirrorCS"),sQuery(id+"F1.wireOp",EDGE,"E7.MirrorCS"),sQuery(id+"F1.wireOp",EDGE,"E8"),sQuery(id+"F1.wireOp",EDGE,"E9"),sQuery(id+"F1.wireOp",EDGE,"E10"),sQuery(id+"F1.wireOp",EDGE,"E11")])]});
            hole(context, id + "F30", {"style" : HoleStyle.SIMPLE, "endStyle" : HoleEndStyle.BLIND, "standardTappedOrClearance" : lookupTablePath({ "standard" : "ISO", "engagement" : "75%", "pitch" : "0.6 mm", "size" : "M3", "type" : "Tapped" }), "standardBlindInLast" : lookupTablePath({ "standard" : "ISO", "engagement" : "75%", "pitch" : "0.6 mm", "size" : "M3", "type" : "Tapped" }), "holeDiameter" : 2.4 * mm, "holeDepth" : 2.5 * mm, "locations" : qUnion([Q0, Q1]), "scope" : qUnion([Q2]), "startStyle" : HoleStartStyle.SKETCH});
        }
    });
